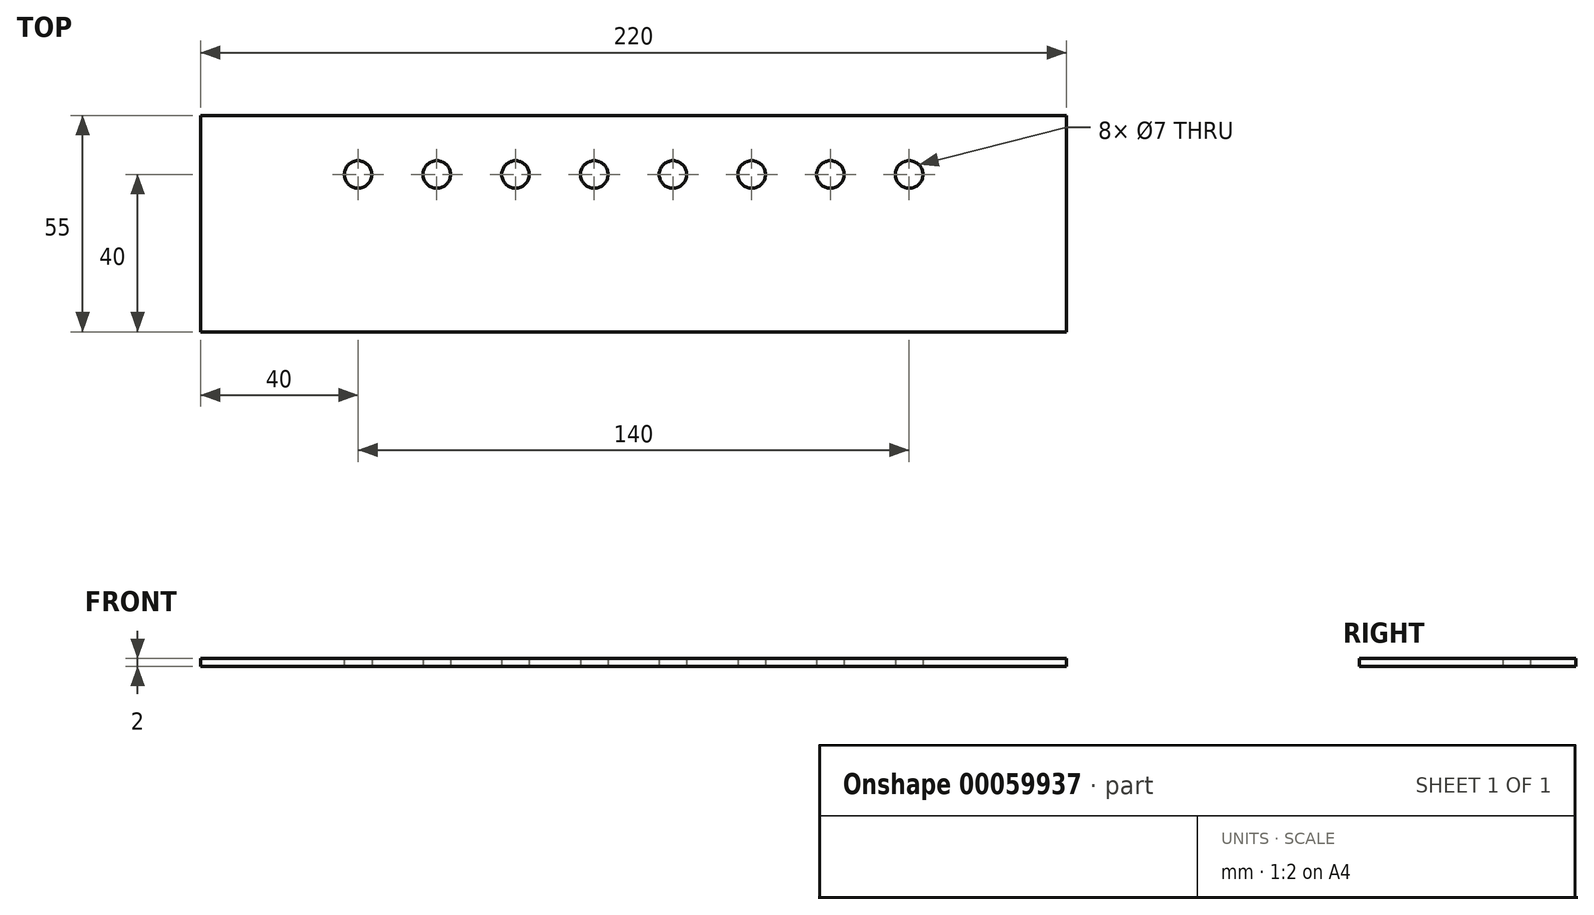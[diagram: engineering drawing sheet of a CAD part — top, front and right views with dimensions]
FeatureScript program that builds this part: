
annotation { "Feature Type Name" : "Feature", "Feature Type Description" : "" }
export const myFeature = defineFeature(function(context is Context, id is Id, definition is map)
    precondition{}
    {
        {
            var Q0;
            Q0=qCreatedBy(makeId("Top.planeOp"),FACE);
            var sketch = newSketch(context, id + "F0", { "sketchPlane" : qUnion([Q0])});
            skLineSegment(sketch, "E0.bottom", {"start": v(0, 0) * mm, "end": v(220, 0) * mm});
            skLineSegment(sketch, "E0.top", {"start": v(0, 55) * mm, "end": v(220, 55) * mm});
            skLineSegment(sketch, "E0.left", {"start": v(0, 0) * mm, "end": v(0, 55) * mm});
            skLineSegment(sketch, "E0.right", {"start": v(220, 0) * mm, "end": v(220, 55) * mm});
            skCircle(sketch, "E1", {"center": v(40, 40) * mm, "radius": 3.5 * mm});
            skCircle(sketch, "E2.1.0.0", {"center": v(60, 40) * mm, "radius": 3.5 * mm});
            skCircle(sketch, "E2.2.0.0", {"center": v(80, 40) * mm, "radius": 3.5 * mm});
            skCircle(sketch, "E2.3.0.0", {"center": v(100, 40) * mm, "radius": 3.5 * mm});
            skCircle(sketch, "E2.4.0.0", {"center": v(120, 40) * mm, "radius": 3.5 * mm});
            skCircle(sketch, "E2.5.0.0", {"center": v(140, 40) * mm, "radius": 3.5 * mm});
            skCircle(sketch, "E2.6.0.0", {"center": v(160, 40) * mm, "radius": 3.5 * mm});
            skCircle(sketch, "E2.7.0.0", {"center": v(180, 40) * mm, "radius": 3.5 * mm});
            skLineSegment(sketch, "E2.direction1", {"start": v(40, 40) * mm, "end": v(60, 40) * mm, "construction": true});
            skLineSegment(sketch, "E3", {"start": v(0, 40) * mm, "end": v(40, 40) * mm, "construction": true});
            skLineSegment(sketch, "E4", {"start": v(180, 40) * mm, "end": v(220, 40) * mm, "construction": true});
            skSolve(sketch);
        }
        {
            var Q0;
            Q0=makeQuery(id+"F0.imprint","IMPRINT",FACE,{"disambiguationData":[TD([[makeQuery(id+"F0.imprint","IMPRINT",EDGE,{"derivedFrom":sQuery(id+"F0.wireOp",EDGE,"E0.bottom")}),1.0]])]});
            extrude(context, id + "F1", {"entities" : qUnion([Q0]), "depth" : 2 * mm});
        }
    });
